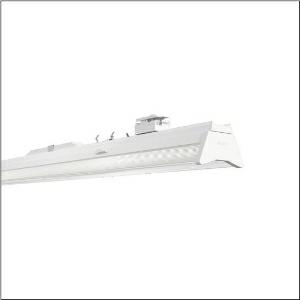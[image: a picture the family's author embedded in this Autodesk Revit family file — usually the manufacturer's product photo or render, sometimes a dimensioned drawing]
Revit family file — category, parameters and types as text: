
# Revit family: licross_r__21_performance_mo_52td16cn66xg_bcc0
name_source: partatom
category: Lighting Fixtures
units: mm (PartAtom-declared; Revit-internal decimal feet)

## family parameters
Cut with Voids When Loaded = No
Host = Face
Light Source = No
Part Type = Normal
Room Calculation Point = No
Round Connector Dimension = Use Diameter
Shared = No

## types (1)
- --- (1 x LED, 5970 lm, 32.8 W, 6500K)
    Apparent Load = 33 VA
    CIE Flux Codes = 66 88 96 79 100
    Color Rendering = 80
    Color Temperature = 6500K
    Default Elevation = 1800 mm
    Description = Licross® 21 Performance MO, luminaire insert, of sheet steel, galvanised, coil coated, white, length: 1.500mm, width: 120mm, height: 123mm, LED rated luminous flux: 5.970lm, light colour: 865, control gear: ON/OFF Multilumen, CLOi, with plug, 3-pole, with phase selection, mains connection: 220..240V, AC, 50/60Hz, start of lifetime: 33W, end of service life: 39W, internal wiring halogen-free, primary light control with lens, of plastic, primary optical cover: cover, of PMMA, light emission: direct/indirect distribution, primary light characteristic: symmetric, protection rating (complete): IP54, insulation class (complete): insulation class I (protective earthing), certification: CE, ENEC, UKCA, protection symbol: D if used in an environment with non-conductive dust loads with corresponding accessories, impact resistance: IK06, permissible ambient temperature for indoor applications: -35..+55°C, corresponds to IFS (International Featured Standards) requirements for safety and quality in the food industry, reducing of maximum allowable ambient temperature of 5°C with ceiling mounting, LABS conformity tested according to VDMA 24364:2018-05, packaging unit: 1 piece
    Height = 114 mm
    Lamp = 1 x LED
    Lamp Light Flux = 5970 lm
    Lamp Power = 32.8 W
    Lamp count = 1
    Length = 1500 mm
    Luminous efficacy = 182 lm/W
    Manufacturer = Siteco
    ModVariant = No
    Model = 52TD16CN66XG
    Mounting Place = Ceiling
    Mounting Type = Pendant
    Number of Poles = 1
    OnlyDefault = Yes
    Power Factor = 1
    Product Name = Licross® 21 Performance MO
    Product group = luminaire insert | ceiling pendant
    ProductGroupID = 902
    Protection Class = Protection class I
    Protection Degree = IP 54
    RLX_Detail_Level = 1
    RLX_Emergency_Light_Flux = 0 lm
    RLX_Emergency_Type = 0
    RLX_Emergency_Type_DB = No
    RlxData = <blob elided: 31853 chars, md5=4cd43ab2>
    Socket = socket
    Standby Power = 0 W
    System Light Flux = 5970 lm
    System Power = 33 W
    Type Comments = factory setting: luminous flux: 100 % | (A | C | E) | 76 mA
    Type Image = l_1256138.jpg
    URL = http://relux.com
    VarID = @adj_069855
    Voltage = 0 V
    Weight = 0.00 kg
    Width = 120 mm

## geometry (parser evidence)
native form markers: Blend x4, Sweep x11
no freeform markers — native parametric forms only
